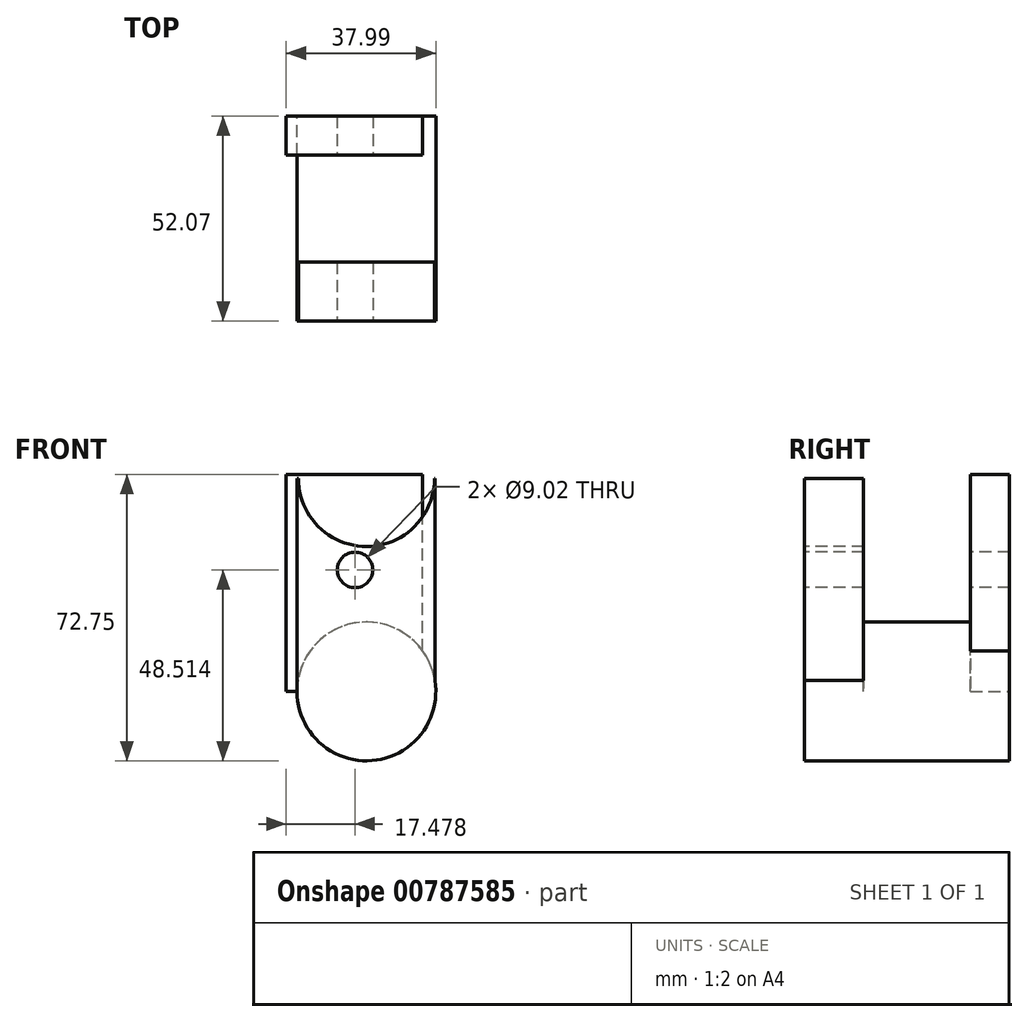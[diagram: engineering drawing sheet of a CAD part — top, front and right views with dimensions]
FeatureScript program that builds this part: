
annotation { "Feature Type Name" : "Feature", "Feature Type Description" : "" }
export const myFeature = defineFeature(function(context is Context, id is Id, definition is map)
    precondition{}
    {
        {
            var Q0;
            Q0=qCreatedBy(makeId("Front.planeOp"),FACE);
            var sketch = newSketch(context, id + "F0", { "sketchPlane" : qUnion([Q0])});
            skCircle(sketch, "E0", {"center": v(0, 0) * mm, "radius": 17.63 * mm});
            skSolve(sketch);
        }
        {
            var Q0;
            Q0=makeQuery(id+"F0.imprint","IMPRINT",FACE,{"disambiguationData":[TD([[makeQuery(id+"F0.imprint","IMPRINT",EDGE,{"derivedFrom":sQuery(id+"F0.wireOp",EDGE,"E0")}),1.0]])]});
            extrude(context, id + "F1", {"entities" : qUnion([Q0]), "depth" : 52.07 * mm, "offsetDistance" : 25.4 * mm});
        }
        {
            var Q0;
            Q0=qCreatedBy(makeId("Front.planeOp"),FACE);
            var sketch = newSketch(context, id + "F2", { "sketchPlane" : qUnion([Q0])});
            skLineSegment(sketch, "E1.bottom", {"start": v(-20.36, 0) * mm, "end": v(14.32, 0) * mm});
            skLineSegment(sketch, "E1.top", {"start": v(-20.36, 55.12) * mm, "end": v(14.32, 55.12) * mm});
            skLineSegment(sketch, "E1.left", {"start": v(-20.36, 0) * mm, "end": v(-20.36, 55.12) * mm});
            skLineSegment(sketch, "E1.right", {"start": v(14.32, 0) * mm, "end": v(14.32, 55.12) * mm});
            skSolve(sketch);
        }
        {
            var Q0;
            Q0=makeQuery(id+"F1.opExtrude","CAP_FACE",FACE,{"disambiguationData":[OSD([sQuery(id+"F0.wireOp",EDGE,"E0")])],"isStart":false});
            var sketch = newSketch(context, id + "F3", { "sketchPlane" : qUnion([Q0])});
            skLineSegment(sketch, "E2.bottom", {"start": v(-17.63, 0) * mm, "end": v(17.4, 0) * mm});
            skLineSegment(sketch, "E2.top", {"start": v(-17.63, 54.16) * mm, "end": v(17.4, 54.16) * mm});
            skLineSegment(sketch, "E2.left", {"start": v(-17.63, 0) * mm, "end": v(-17.63, 54.16) * mm});
            skLineSegment(sketch, "E2.right", {"start": v(17.4, 0) * mm, "end": v(17.4, 54.16) * mm});
            skSolve(sketch);
        }
        {
            var Q0;
            {var subQ0=sQuery(id+"F3.wireOp",EDGE,"E2.top");Q0=makeQuery(id+"F3.imprint","IMPRINT",FACE,{"disambiguationData":[TD([[makeQuery(id+"F3.imprint","IMPRINT",EDGE,{"derivedFrom":subQ0}),-1.0]])]});}
            var sketch = newSketch(context, id + "F4", { "sketchPlane" : qUnion([Q0])});
            skCircle(sketch, "E3", {"center": v(0, 54.13) * mm, "radius": 17.3 * mm});
            skSolve(sketch);
        }
        {
            var Q0;
            Q0=makeQuery(id+"F2.imprint","IMPRINT",FACE,{"disambiguationData":[TD([[makeQuery(id+"F2.imprint","IMPRINT",EDGE,{"derivedFrom":sQuery(id+"F2.wireOp",EDGE,"E1.bottom")}),1.0]])]});
            var sketch = newSketch(context, id + "F5", { "sketchPlane" : qUnion([Q0])});
            skCircle(sketch, "E4", {"center": v(0, 55.15) * mm, "radius": 14.38 * mm});
            skSolve(sketch);
        }
        {
            var Q0;
            {var subQ0=sQuery(id+"F3.wireOp",EDGE,"E2.left");var subQ6=makeQuery(id+"F3.imprint","IMPRINT",EDGE,{"derivedFrom":subQ0});Q0=makeQuery(id+"F4.imprint","IMPRINT",FACE,{"disambiguationData":[TD([[makeQuery(id+"F4.imprint","IMPRINT",EDGE,{"derivedFrom":subQ6}),-1.0]])]});}
            extrude(context, id + "F6", {"entities" : qUnion([Q0]), "operationType" : NewBodyOperationType.ADD, "oppositeDirection" : true, "depth" : 15 * mm, "offsetDistance" : 25.4 * mm});
        }
        {
            var Q0;
            {var subQ4=makeQuery(id+"F2.imprint","IMPRINT",EDGE,{"derivedFrom":sQuery(id+"F2.wireOp",EDGE,"E1.bottom")});Q0=makeQuery(id+"F5.imprint","IMPRINT",FACE,{"disambiguationData":[TD([[makeQuery(id+"F5.imprint","IMPRINT",EDGE,{"derivedFrom":subQ4}),1.0]])]});}
            var Q1;
            Q1=makeQuery(id+"F2.imprint","IMPRINT",FACE,{"disambiguationData":[TD([[makeQuery(id+"F2.imprint","IMPRINT",EDGE,{"derivedFrom":sQuery(id+"F2.wireOp",EDGE,"E1.bottom")}),1.0]])]});
            extrude(context, id + "F7", {"entities" : qUnion([Q0, Q1]), "operationType" : NewBodyOperationType.ADD, "depth" : 9.9 * mm, "offsetDistance" : 25.4 * mm});
        }
        {
            var Q0;
            {var subQ0=sQuery(id+"F3.wireOp",EDGE,"E2.top");Q0=makeQuery(id+"F3.imprint","IMPRINT",FACE,{"disambiguationData":[TD([[makeQuery(id+"F3.imprint","IMPRINT",EDGE,{"derivedFrom":subQ0}),-1.0]])]});}
            var sketch = newSketch(context, id + "F8", { "sketchPlane" : qUnion([Q0])});
            skCircle(sketch, "E5", {"center": v(-2.88, 30.88) * mm, "radius": 4.51 * mm});
            skSolve(sketch);
        }
        {
            var Q0;
            Q0=makeQuery(id+"F8.imprint","IMPRINT",FACE,{"disambiguationData":[TD([[makeQuery(id+"F8.imprint","IMPRINT",EDGE,{"derivedFrom":sQuery(id+"F8.wireOp",EDGE,"E5")}),1.0]])]});
            extrude(context, id + "F9", {"entities" : qUnion([Q0]), "operationType" : NewBodyOperationType.REMOVE, "oppositeDirection" : true, "depth" : 2514.6 * mm, "offsetDistance" : 25.4 * mm});
        }
    });
